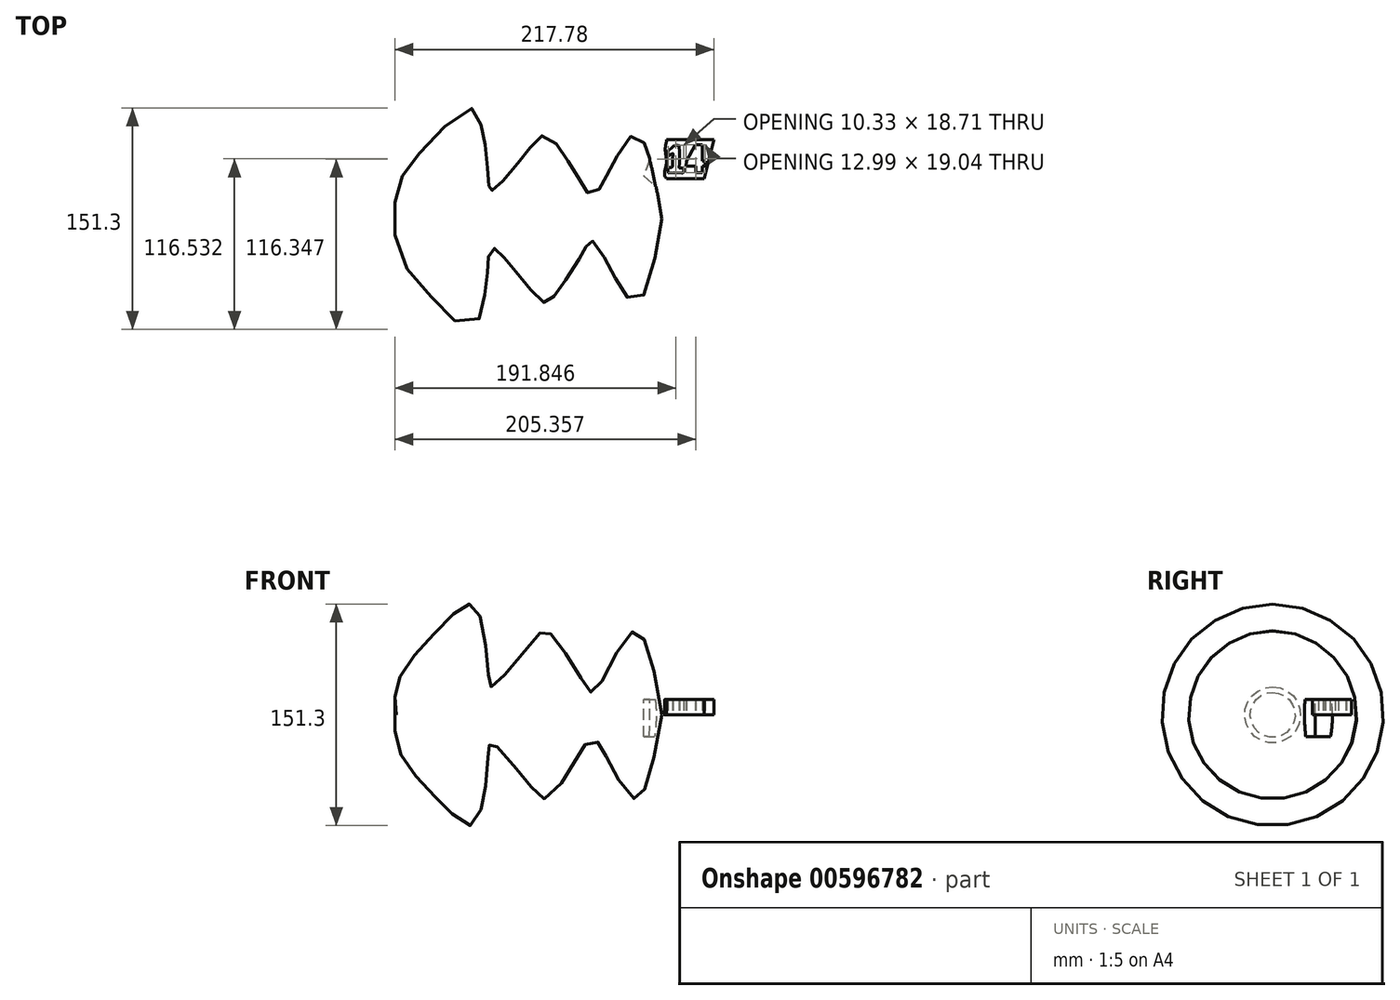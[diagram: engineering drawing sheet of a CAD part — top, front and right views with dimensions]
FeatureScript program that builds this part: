
annotation { "Feature Type Name" : "Feature", "Feature Type Description" : "" }
export const myFeature = defineFeature(function(context is Context, id is Id, definition is map)
    precondition{}
    {
        {
            var Q0;
            Q0=qCreatedBy(makeId("Front.planeOp"),FACE);
            var sketch = newSketch(context, id + "F0", { "sketchPlane" : qUnion([Q0])});
            skLineSegment(sketch, "E0", {"start": v(0, 0) * mm, "end": v(-181.2, 0) * mm});
            skFitSpline(sketch, "E1", {"points": [v(0, 0) * mm, v(-19.73, 56.9) * mm, v(-45.87, 16.12) * mm, v(-52.67, 20.82) * mm, v(-77.24, 56.37) * mm, v(-86.12, 52.71) * mm, v(-115.92, 19.26) * mm, v(-118.54, 27.62) * mm, v(-128.47, 74.67) * mm, v(-147.81, 63.17) * mm, v(-179.7, 23.96) * mm, v(-181.2, 0) * mm], "startDerivative": vector(-122.02, 716.23) * mm, "endDerivative": vector(38.07, -284.46) * mm});
            skSolve(sketch);
        }
        {
            var Q0;
            Q0=makeQuery(id+"F0.imprint","IMPRINT",FACE,{"disambiguationData":[TD([[makeQuery(id+"F0.imprint","IMPRINT",EDGE,{"derivedFrom":sQuery(id+"F0.wireOp",EDGE,"E0")}),-1.0]])]});
            var Q1;
            Q1=sQuery(id+"F0.wireOp",EDGE,"E0");
            revolve(context, id + "F1", {"surfaceOperationType" : NewSurfaceOperationType.NEW, "entities" : qUnion([Q0]), "axis" : qUnion([Q1]), "revolveType" : RevolveType.FULL});
        }
        {
            var Q0;
            Q0=qCreatedBy(makeId("Top.planeOp"),FACE);
            var sketch = newSketch(context, id + "F2", { "sketchPlane" : qUnion([Q0])});
            skFitSpline(sketch, "E2", {"points": [v(4.5, 42.74) * mm, v(4.29, 46.5) * mm, v(4.47, 46.7) * mm, v(6.57, 47.98) * mm, v(8.36, 49.92) * mm, v(11.71, 50.03) * mm, v(11.79, 50.04) * mm, v(11.84, 34.84) * mm, v(11.83, 34.63) * mm, v(14.7, 34.66) * mm, v(14.87, 34.66) * mm, v(14.9, 31.59) * mm, v(14.9, 31.3) * mm, v(4.63, 31.28) * mm, v(4.33, 31.31) * mm, v(4.32, 34.76) * mm, v(4.4, 34.88) * mm, v(7.18, 34.99) * mm, v(7.33, 35) * mm, v(7.5, 44.26) * mm, v(7.55, 45.01) * mm, v(4.5, 42.74) * mm]});
            skFitSpline(sketch, "E3", {"points": [v(34.34, 45.6) * mm, v(35.43, 48) * mm, v(39.16, 50.1) * mm, v(42.67, 50.02) * mm, v(45.3, 48.27) * mm, v(46.09, 45.85) * mm, v(45.6, 42.65) * mm, v(43.41, 41.12) * mm, v(43.5, 41.08) * mm, v(45.1, 40.32) * mm, v(46.41, 37.58) * mm, v(45.98, 34.06) * mm, v(44.53, 32.34) * mm, v(42.12, 31.24) * mm, v(39.52, 31.12) * mm, v(36.88, 31.7) * mm, v(34.5, 34.21) * mm, v(34.01, 36.23) * mm, v(33.9, 36.9) * mm, v(37.43, 37.55) * mm, v(37.74, 37.55) * mm, v(37.95, 36.27) * mm, v(38.4, 35.34) * mm, v(39.83, 34.67) * mm, v(41.22, 35.1) * mm, v(41.88, 36.59) * mm, v(41.82, 37.69) * mm, v(41.47, 38.5) * mm, v(40.7, 39.14) * mm, v(39.45, 39.33) * mm, v(38.47, 39.4) * mm, v(38.11, 39.4) * mm, v(37.95, 42.55) * mm, v(38.18, 42.64) * mm, v(40.27, 42.7) * mm, v(41.65, 44.2) * mm, v(41.53, 45.52) * mm, v(41.07, 46.4) * mm, v(40.55, 46.6) * mm, v(39.88, 46.65) * mm, v(39.27, 46.5) * mm, v(38.92, 46.16) * mm, v(38.57, 45.74) * mm, v(38.3, 45.21) * mm, v(38.16, 44.73) * mm, v(38.04, 44.54) * mm, v(34.29, 45.21) * mm, v(34.24, 45.26) * mm, v(34.34, 45.6) * mm]});
            skLineSegment(sketch, "E4", {"start": v(50.02, 39.1) * mm, "end": v(56.23, 50.27) * mm});
            skLineSegment(sketch, "E5", {"start": v(56.23, 50.27) * mm, "end": v(60.78, 50.27) * mm});
            skLineSegment(sketch, "E6", {"start": v(60.78, 50.27) * mm, "end": v(60.78, 39.18) * mm});
            skLineSegment(sketch, "E7", {"start": v(60.78, 39.18) * mm, "end": v(62.94, 39.18) * mm});
            skLineSegment(sketch, "E8", {"start": v(62.94, 39.18) * mm, "end": v(62.94, 35.77) * mm});
            skLineSegment(sketch, "E9", {"start": v(62.94, 35.77) * mm, "end": v(60.84, 35.77) * mm});
            skLineSegment(sketch, "E10", {"start": v(60.84, 35.77) * mm, "end": v(60.84, 31.24) * mm});
            skLineSegment(sketch, "E11", {"start": v(60.84, 31.24) * mm, "end": v(56.55, 31.24) * mm});
            skLineSegment(sketch, "E12", {"start": v(56.55, 31.24) * mm, "end": v(56.55, 35.65) * mm});
            skLineSegment(sketch, "E13", {"start": v(56.55, 35.65) * mm, "end": v(49.96, 35.65) * mm});
            skLineSegment(sketch, "E14", {"start": v(49.96, 35.65) * mm, "end": v(50.02, 39.1) * mm});
            skLineSegment(sketch, "E15", {"start": v(16.75, 39.23) * mm, "end": v(22.97, 50.4) * mm});
            skLineSegment(sketch, "E16", {"start": v(22.97, 50.4) * mm, "end": v(27.52, 50.4) * mm});
            skLineSegment(sketch, "E17", {"start": v(27.52, 50.4) * mm, "end": v(27.52, 39.3) * mm});
            skLineSegment(sketch, "E18", {"start": v(27.52, 39.3) * mm, "end": v(29.68, 39.3) * mm});
            skLineSegment(sketch, "E19", {"start": v(29.68, 39.3) * mm, "end": v(29.68, 35.9) * mm});
            skLineSegment(sketch, "E20", {"start": v(29.68, 35.9) * mm, "end": v(27.57, 35.9) * mm});
            skLineSegment(sketch, "E21", {"start": v(27.57, 35.9) * mm, "end": v(27.57, 31.36) * mm});
            skLineSegment(sketch, "E22", {"start": v(27.57, 31.36) * mm, "end": v(23.3, 31.36) * mm});
            skLineSegment(sketch, "E23", {"start": v(23.3, 31.36) * mm, "end": v(23.3, 35.77) * mm});
            skLineSegment(sketch, "E24", {"start": v(23.3, 35.77) * mm, "end": v(16.7, 35.77) * mm});
            skLineSegment(sketch, "E25", {"start": v(16.7, 35.77) * mm, "end": v(16.75, 39.23) * mm});
            skSolve(sketch);
        }
        {
            var Q0;
            Q0 = qSketchRegion(id + "F2", true);
            extrude(context, id + "F3", {"entities" : qUnion([Q0]), "depth" : 14.22 * mm, "offsetDistance" : 25.4 * mm});
        }
        {
            var Q0;
            Q0=qCreatedBy(makeId("Top.planeOp"),FACE);
            var sketch = newSketch(context, id + "F4", { "sketchPlane" : qUnion([Q0])});
            skLineSegment(sketch, "E26.bottom", {"start": v(0, 53.98) * mm, "end": v(69.4, 53.98) * mm});
            skLineSegment(sketch, "E26.top", {"start": v(0, 27.3) * mm, "end": v(69.4, 27.3) * mm});
            skLineSegment(sketch, "E26.left", {"start": v(0, 53.98) * mm, "end": v(0, 27.3) * mm});
            skLineSegment(sketch, "E26.right", {"start": v(69.4, 53.98) * mm, "end": v(69.4, 27.3) * mm});
            skSolve(sketch);
        }
        {
            var Q0;
            Q0 = qSketchRegion(id + "F4", true);
            extrude(context, id + "F5", {"entities" : qUnion([Q0]), "depth" : 10.4 * mm, "offsetDistance" : 25.4 * mm});
        }
        {
            var Q0;
            Q0=makeQuery(id+"F3.opExtrude","SWEPT_BODY",BODY,{"disambiguationData":[OSD([sQuery(id+"F2.wireOp",EDGE,"E2")])]});
            var Q1;
            Q1=makeQuery(id+"F3.opExtrude","SWEPT_BODY",BODY,{"disambiguationData":[OSD([sQuery(id+"F2.wireOp",EDGE,"E15"),sQuery(id+"F2.wireOp",EDGE,"E16"),sQuery(id+"F2.wireOp",EDGE,"E17"),sQuery(id+"F2.wireOp",EDGE,"E18"),sQuery(id+"F2.wireOp",EDGE,"E19"),sQuery(id+"F2.wireOp",EDGE,"E20"),sQuery(id+"F2.wireOp",EDGE,"E21"),sQuery(id+"F2.wireOp",EDGE,"E22"),sQuery(id+"F2.wireOp",EDGE,"E23"),sQuery(id+"F2.wireOp",EDGE,"E24"),sQuery(id+"F2.wireOp",EDGE,"E25")])]});
            var Q2;
            Q2=makeQuery(id+"F3.opExtrude","SWEPT_BODY",BODY,{"disambiguationData":[OSD([sQuery(id+"F2.wireOp",EDGE,"E3")])]});
            var Q3;
            Q3=makeQuery(id+"F3.opExtrude","SWEPT_BODY",BODY,{"disambiguationData":[OSD([sQuery(id+"F2.wireOp",EDGE,"E4"),sQuery(id+"F2.wireOp",EDGE,"E5"),sQuery(id+"F2.wireOp",EDGE,"E6"),sQuery(id+"F2.wireOp",EDGE,"E7"),sQuery(id+"F2.wireOp",EDGE,"E8"),sQuery(id+"F2.wireOp",EDGE,"E9"),sQuery(id+"F2.wireOp",EDGE,"E10"),sQuery(id+"F2.wireOp",EDGE,"E11"),sQuery(id+"F2.wireOp",EDGE,"E12"),sQuery(id+"F2.wireOp",EDGE,"E13"),sQuery(id+"F2.wireOp",EDGE,"E14")])]});
            var Q4;
            Q4=makeQuery(id+"F5.opExtrude","SWEPT_BODY",BODY,{"disambiguationData":[OSD([sQuery(id+"F4.wireOp",EDGE,"E26.bottom"),sQuery(id+"F4.wireOp",EDGE,"E26.top"),sQuery(id+"F4.wireOp",EDGE,"E26.left"),sQuery(id+"F4.wireOp",EDGE,"E26.right")])]});
            booleanBodies(context, id + "F6", {"operationType" : BooleanOperationType.SUBTRACTION, "tools" : qUnion([Q0, Q1, Q2, Q3]), "targets" : qUnion([Q4])});
        }
        {
            var Q0;
            Q0=makeQuery(id+"F5.opExtrude","CAP_FACE",FACE,{"disambiguationData":[OSD([sQuery(id+"F4.wireOp",EDGE,"E26.bottom"),sQuery(id+"F4.wireOp",EDGE,"E26.top"),sQuery(id+"F4.wireOp",EDGE,"E26.left"),sQuery(id+"F4.wireOp",EDGE,"E26.right")])],"isStart":false});
            var sketch = newSketch(context, id + "F7", { "sketchPlane" : qUnion([Q0])});
            skLineSegment(sketch, "E27", {"start": v(34.7, 53.98) * mm, "end": v(29.68, 27.3) * mm});
            skPoint(sketch, "E28.0.internal.snap0", {"position": v(53.12, 44.69) * mm});
            skFitSpline(sketch, "E28", {"points": [v(53.12, 53.98) * mm, v(48.58, 43.92) * mm, v(47.89, 30.44) * mm, v(44.9, 27.3) * mm], "startDerivative": vector(-16.13, -24.36) * mm, "endDerivative": vector(-15.83, -9.53) * mm});
            skFitSpline(sketch, "E29", {"points": [v(3.32, 53.98) * mm, v(2.38, 46.46) * mm, v(3.21, 38.34) * mm, v(1.88, 29.86) * mm, v(3.33, 27.3) * mm], "startDerivative": vector(-6.03, -28.08) * mm, "endDerivative": vector(11.88, -12.4) * mm});
            skLineSegment(sketch, "E30", {"start": v(3.32, 53.98) * mm, "end": v(-0.85, 60.91) * mm});
            skLineSegment(sketch, "E31", {"start": v(-0.85, 60.91) * mm, "end": v(-12.34, 29.15) * mm});
            skLineSegment(sketch, "E32", {"start": v(-12.34, 29.15) * mm, "end": v(-1.42, 19.57) * mm});
            skLineSegment(sketch, "E33", {"start": v(-1.42, 19.57) * mm, "end": v(3.33, 27.3) * mm});
            skSolve(sketch);
        }
        {
            var Q0;
            {var subQ1=sQuery(id+"F7.wireOp",EDGE,"E30");Q0=makeQuery(id+"F7.imprint","IMPRINT",FACE,{"disambiguationData":[TD([[makeQuery(id+"F7.imprint","IMPRINT",EDGE,{"derivedFrom":subQ1}),1.0]])]});}
            extrude(context, id + "F8", {"entities" : qUnion([Q0]), "operationType" : NewBodyOperationType.REMOVE, "oppositeDirection" : true, "depth" : 25.4 * mm, "offsetDistance" : 25.4 * mm});
        }
        {
            var Q0;
            Q0 = qSketchRegion(id + "F7", true);
            extrude(context, id + "F9", {"entities" : qUnion([Q0]), "operationType" : NewBodyOperationType.REMOVE, "oppositeDirection" : true, "depth" : 25.4 * mm, "offsetDistance" : 25.4 * mm});
        }
        {
            var Q0;
            Q0=makeQuery(id+"F5.opExtrude","CAP_FACE",FACE,{"disambiguationData":[OSD([sQuery(id+"F4.wireOp",EDGE,"E26.bottom"),sQuery(id+"F4.wireOp",EDGE,"E26.top"),sQuery(id+"F4.wireOp",EDGE,"E26.left"),sQuery(id+"F4.wireOp",EDGE,"E26.right")])],"isStart":false});
            var sketch = newSketch(context, id + "F10", { "sketchPlane" : qUnion([Q0])});
            skFitSpline(sketch, "E34", {"points": [v(67.9, 53.98) * mm, v(64.46, 43.8) * mm, v(67.9, 35.87) * mm, v(65.81, 27.3) * mm], "startDerivative": vector(-16.56, -29.7) * mm, "endDerivative": vector(-12.34, -27.23) * mm});
            skLineSegment(sketch, "E35", {"start": v(65.81, 27.3) * mm, "end": v(73.22, 22.31) * mm});
            skLineSegment(sketch, "E36", {"start": v(73.22, 22.31) * mm, "end": v(76.35, 31.07) * mm});
            skLineSegment(sketch, "E37", {"start": v(76.35, 31.07) * mm, "end": v(72.7, 58.4) * mm});
            skLineSegment(sketch, "E38", {"start": v(72.7, 58.4) * mm, "end": v(69.47, 55.38) * mm});
            skLineSegment(sketch, "E39", {"start": v(69.47, 55.38) * mm, "end": v(67.9, 53.98) * mm});
            skSolve(sketch);
        }
        {
            var Q0;
            {var subQ0=sQuery(id+"F10.wireOp",EDGE,"E34");Q0=makeQuery(id+"F10.imprint","IMPRINT",FACE,{"disambiguationData":[TD([[makeQuery(id+"F10.imprint","IMPRINT",EDGE,{"derivedFrom":subQ0}),1.0]])]});}
            extrude(context, id + "F11", {"entities" : qUnion([Q0]), "operationType" : NewBodyOperationType.REMOVE, "oppositeDirection" : true, "depth" : 25.4 * mm, "offsetDistance" : 25.4 * mm});
        }
        {
            var Q0;
            Q0=makeQuery(id+"F5.opExtrude","CAP_FACE",FACE,{"disambiguationData":[OSD([sQuery(id+"F4.wireOp",EDGE,"E26.bottom"),sQuery(id+"F4.wireOp",EDGE,"E26.top"),sQuery(id+"F4.wireOp",EDGE,"E26.left"),sQuery(id+"F4.wireOp",EDGE,"E26.right")])],"isStart":false});
            var sketch = newSketch(context, id + "F12", { "sketchPlane" : qUnion([Q0])});
            skLineSegment(sketch, "E40", {"start": v(35.61, 53.98) * mm, "end": v(29.08, 27.3) * mm});
            skLineSegment(sketch, "E41", {"start": v(29.08, 27.3) * mm, "end": v(79.7, 3.35) * mm});
            skLineSegment(sketch, "E42", {"start": v(79.7, 3.35) * mm, "end": v(81.47, 21.3) * mm});
            skLineSegment(sketch, "E43", {"start": v(81.47, 21.3) * mm, "end": v(80.93, 63.66) * mm});
            skLineSegment(sketch, "E44", {"start": v(80.93, 63.66) * mm, "end": v(35.61, 53.98) * mm});
            skSolve(sketch);
        }
        {
            var Q0;
            Q0 = qSketchRegion(id + "F12", true);
            extrude(context, id + "F13", {"entities" : qUnion([Q0]), "operationType" : NewBodyOperationType.REMOVE, "oppositeDirection" : true, "depth" : 25.4 * mm, "offsetDistance" : 25.4 * mm});
        }
    });
